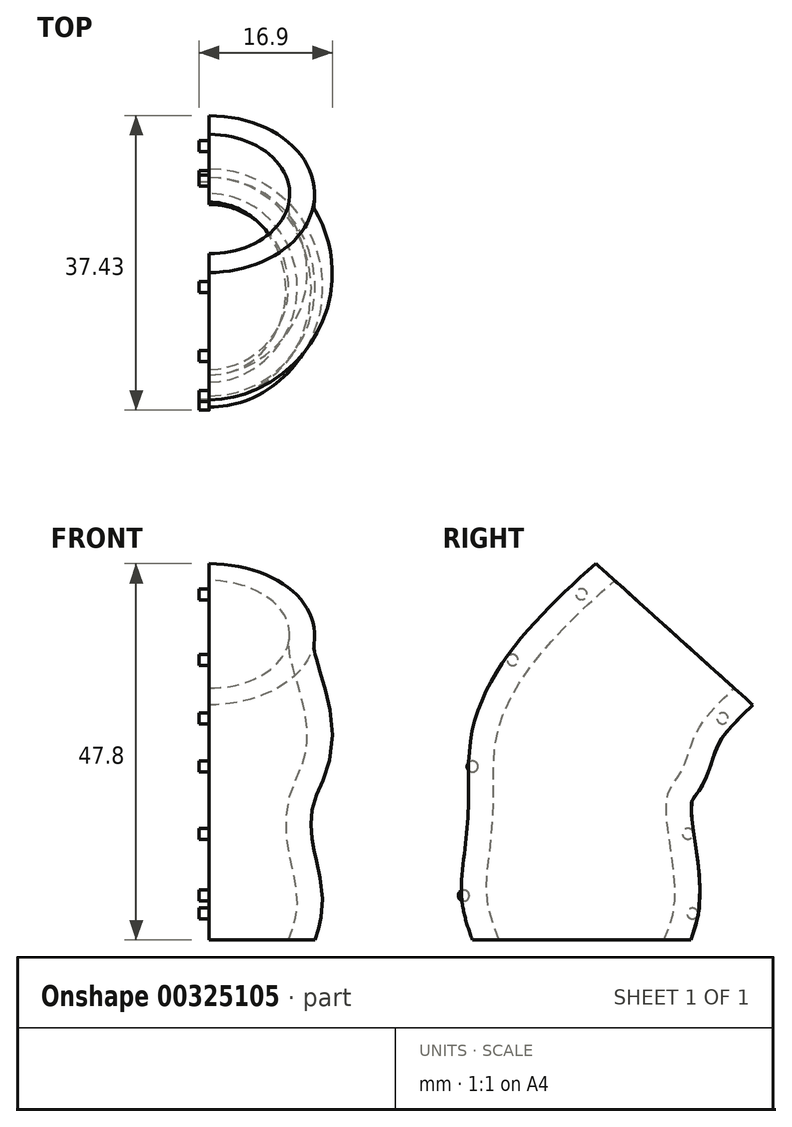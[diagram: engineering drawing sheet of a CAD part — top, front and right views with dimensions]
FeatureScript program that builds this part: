
annotation { "Feature Type Name" : "Feature", "Feature Type Description" : "" }
export const myFeature = defineFeature(function(context is Context, id is Id, definition is map)
    precondition{}
    {
        {
            var Q0;
            Q0=qCreatedBy(makeId("Top.planeOp"),FACE);
            var sketch = newSketch(context, id + "F0", { "sketchPlane" : qUnion([Q0])});
            skEllipse(sketch, "E0", {"center": v(0, 0) * mm, "majorRadius": 10.48 * mm, "minorRadius": 10.06 * mm, "majorAxis": v(0, 1)});
            skSolve(sketch);
        }
        {
            var Q0;
            Q0=qCreatedBy(makeId("Top.planeOp"),FACE);
            cPlane(context, id + "F1", {"entities" : qUnion([Q0]), "cplaneType" : CPlaneType.OFFSET, "offset" : 3.17 * mm, "width" : 152.4 * mm, "height" : 152.4 * mm});
        }
        {
            var Q0;
            Q0=qCreatedBy(id+"F1.planeOp",FACE);
            var sketch = newSketch(context, id + "F2", { "sketchPlane" : qUnion([Q0])});
            skEllipse(sketch, "E1", {"center": v(0, 0) * mm, "majorRadius": 11.6 * mm, "minorRadius": 11.04 * mm, "majorAxis": v(0, 1)});
            skSolve(sketch);
        }
        {
            var Q0;
            Q0=qCreatedBy(makeId("Top.planeOp"),FACE);
            cPlane(context, id + "F3", {"entities" : qUnion([Q0]), "cplaneType" : CPlaneType.OFFSET, "offset" : 19.05 * mm, "width" : 152.4 * mm, "height" : 152.4 * mm});
        }
        {
            var Q0;
            Q0=qCreatedBy(id+"F3.planeOp",FACE);
            var sketch = newSketch(context, id + "F4", { "sketchPlane" : qUnion([Q0])});
            skEllipse(sketch, "E2", {"center": v(0, 0) * mm, "majorRadius": 11.18 * mm, "minorRadius": 10.48 * mm, "majorAxis": v(0, -1)});
            skSolve(sketch);
        }
        {
            var Q0;
            Q0=qCreatedBy(makeId("Right.planeOp"),FACE);
            var sketch = newSketch(context, id + "F5", { "sketchPlane" : qUnion([Q0])});
            skLineSegment(sketch, "E3", {"start": v(-8.35, 25.4) * mm, "end": v(9.56, 21.59) * mm});
            skSolve(sketch);
        }
        {
            var Q0;
            Q0=qCreatedBy(makeId("Right.planeOp"),FACE);
            var Q1;
            Q1 = qBodyType(qCreatedBy(id + "F5" ,EDGE), BodyType.WIRE);
            cPlane(context, id + "F6", {"entities" : qUnion([Q0, Q1]), "cplaneType" : CPlaneType.LINE_ANGLE, "offset" : 25.4 * mm, "angle" : 90 * degree, "width" : 152.4 * mm, "height" : 152.4 * mm});
        }
        {
            var Q0;
            Q0=qCreatedBy(id+"F6.planeOp",FACE);
            var sketch = newSketch(context, id + "F7", { "sketchPlane" : qUnion([Q0])});
            skEllipse(sketch, "E4", {"center": v(0, -4.06) * mm, "majorRadius": 11.87 * mm, "minorRadius": 12.15 * mm, "majorAxis": v(0, 1)});
            skSolve(sketch);
        }
        {
            var Q0;
            Q0=qCreatedBy(id+"F6.planeOp",FACE);
            var sketch = newSketch(context, id + "F8", { "sketchPlane" : qUnion([Q0])});
            skLineSegment(sketch, "E5", {"start": v(11.1, -4.63) * mm, "end": v(-10.76, -4.63) * mm});
            skSolve(sketch);
        }
        {
            var Q0;
            Q0=sQuery(id+"F8.wireOp",EDGE,"E5");
            var Q1;
            Q1=qCreatedBy(id+"F6.planeOp",FACE);
            cPlane(context, id + "F9", {"entities" : qUnion([Q0, Q1]), "cplaneType" : CPlaneType.LINE_ANGLE, "offset" : 25.4 * mm, "angle" : 30 * degree, "width" : 152.4 * mm, "height" : 152.4 * mm});
        }
        {
            var Q0;
            Q0=qCreatedBy(id+"F9.planeOp",FACE);
            cPlane(context, id + "F10", {"entities" : qUnion([Q0]), "cplaneType" : CPlaneType.OFFSET, "offset" : 12.7 * mm, "oppositeDirection" : true, "width" : 152.4 * mm, "height" : 152.4 * mm});
        }
        {
            var Q0;
            Q0=qCreatedBy(id+"F10.planeOp",FACE);
            var sketch = newSketch(context, id + "F11", { "sketchPlane" : qUnion([Q0])});
            skCircle(sketch, "E6", {"center": v(0, 17.54) * mm, "radius": 10.52 * mm});
            skSolve(sketch);
        }
        {
            var Q0;
            Q0=qCreatedBy(id+"F9.planeOp",FACE);
            cPlane(context, id + "F12", {"entities" : qUnion([Q0]), "cplaneType" : CPlaneType.OFFSET, "offset" : 19.05 * mm, "oppositeDirection" : true, "width" : 152.4 * mm, "height" : 152.4 * mm});
        }
        {
            var Q0;
            Q0=qCreatedBy(id+"F12.planeOp",FACE);
            var sketch = newSketch(context, id + "F13", { "sketchPlane" : qUnion([Q0])});
            skCircle(sketch, "E7", {"center": v(0, 17.21) * mm, "radius": 10.21 * mm});
            skSolve(sketch);
        }
        {
            var Q0;
            Q0 = qSketchRegion(id + "F0", true);
            var Q1;
            Q1 = qSketchRegion(id + "F2", true);
            var Q2;
            Q2 = qSketchRegion(id + "F4", true);
            var Q3;
            Q3=makeQuery(id+"F7.imprint","IMPRINT",FACE,{"disambiguationData":[TD([[makeQuery(id+"F7.imprint","IMPRINT",EDGE,{"derivedFrom":sQuery(id+"F7.wireOp",EDGE,"E4")}),1.0]])]});
            var Q4;
            Q4 = qSketchRegion(id + "F11", true);
            var Q5;
            Q5 = qSketchRegion(id + "F13", true);
            loft(context, id + "F14", {"sheetProfilesArray" : [{ "sheetProfileEntities" : qUnion([Q0]) }, { "sheetProfileEntities" : qUnion([Q1]) }, { "sheetProfileEntities" : qUnion([Q2]) }, { "sheetProfileEntities" : qUnion([Q3]) }, { "sheetProfileEntities" : qUnion([Q4]) }, { "sheetProfileEntities" : qUnion([Q5]) }]});
        }
        {
            var Q0;
            Q0=makeQuery(id+"F14.opLoft","CAP_FACE",FACE,{"disambiguationData":[OSD([makeQuery(id+"F13.imprint","IMPRINT",FACE,{"disambiguationData":[TD([[makeQuery(id+"F13.imprint","IMPRINT",EDGE,{"derivedFrom":sQuery(id+"F13.wireOp",EDGE,"E7")}),1.0]])]})])],"isStart":true});
            var Q1;
            Q1=makeQuery(id+"F14.opLoft","CAP_FACE",FACE,{"disambiguationData":[OSD([makeQuery(id+"F0.imprint","IMPRINT",FACE,{"disambiguationData":[TD([[makeQuery(id+"F0.imprint","IMPRINT",EDGE,{"derivedFrom":sQuery(id+"F0.wireOp",EDGE,"E0")}),1.0]])]})])],"isStart":true});
            var Q2;
            Q2=makeQuery(id+"F14.opLoft","SWEPT_BODY",BODY,{"disambiguationData":[OSD([makeQuery(id+"F0.imprint","IMPRINT",FACE,{"disambiguationData":[TD([[makeQuery(id+"F0.imprint","IMPRINT",EDGE,{"derivedFrom":sQuery(id+"F0.wireOp",EDGE,"E0")}),1.0]])]}),sQuery(id+"F2.wireOp",EDGE,"E1"),sQuery(id+"F4.wireOp",EDGE,"E2"),sQuery(id+"F7.wireOp",EDGE,"E4"),sQuery(id+"F11.wireOp",EDGE,"E6"),makeQuery(id+"F13.imprint","IMPRINT",FACE,{"disambiguationData":[TD([[makeQuery(id+"F13.imprint","IMPRINT",EDGE,{"derivedFrom":sQuery(id+"F13.wireOp",EDGE,"E7")}),1.0]])]})])]});
            shell(context, id + "F15", {"entities" : qUnion([Q0, Q1]), "parts" : qUnion([Q2]), "thickness" : 3.17 * mm, "oppositeDirection" : true});
        }
        {
            var Q0;
            Q0=makeQuery(id+"F14.opLoft","SWEPT_BODY",BODY,{"disambiguationData":[OSD([makeQuery(id+"F0.imprint","IMPRINT",FACE,{"disambiguationData":[TD([[makeQuery(id+"F0.imprint","IMPRINT",EDGE,{"derivedFrom":sQuery(id+"F0.wireOp",EDGE,"E0")}),1.0]])]}),sQuery(id+"F2.wireOp",EDGE,"E1"),sQuery(id+"F4.wireOp",EDGE,"E2"),sQuery(id+"F7.wireOp",EDGE,"E4"),sQuery(id+"F11.wireOp",EDGE,"E6"),makeQuery(id+"F13.imprint","IMPRINT",FACE,{"disambiguationData":[TD([[makeQuery(id+"F13.imprint","IMPRINT",EDGE,{"derivedFrom":sQuery(id+"F13.wireOp",EDGE,"E7")}),1.0]])]})])]});
            transform(context, id + "F16", {"entities" : qUnion([Q0]), "transformType" : TransformType.TRANSLATION_3D, "dx" : 32 * mm, "dy" : 0 * mm, "dz" : 0 * mm, "makeCopy" : true});
        }
        {
            var Q0;
            Q0=makeQuery(id+"F16.opPattern","COPY",BODY,{"derivedFrom":makeQuery(id+"F14.opLoft","SWEPT_BODY",BODY,{"disambiguationData":[OSD([makeQuery(id+"F0.imprint","IMPRINT",FACE,{"disambiguationData":[TD([[makeQuery(id+"F0.imprint","IMPRINT",EDGE,{"derivedFrom":sQuery(id+"F0.wireOp",EDGE,"E0")}),1.0]])]}),sQuery(id+"F2.wireOp",EDGE,"E1"),sQuery(id+"F4.wireOp",EDGE,"E2"),sQuery(id+"F7.wireOp",EDGE,"E4"),sQuery(id+"F11.wireOp",EDGE,"E6"),makeQuery(id+"F13.imprint","IMPRINT",FACE,{"disambiguationData":[TD([[makeQuery(id+"F13.imprint","IMPRINT",EDGE,{"derivedFrom":sQuery(id+"F13.wireOp",EDGE,"E7")}),1.0]])]})])]}),"instanceName":"1"});
            deleteBodies(context, id + "F17", {"entities" : qUnion([Q0])});
        }
        {
            var Q0;
            Q0=qCreatedBy(makeId("Right.planeOp"),FACE);
            var sketch = newSketch(context, id + "F18", { "sketchPlane" : qUnion([Q0])});
            skCircle(sketch, "E8", {"center": v(2.37, 23.36) * mm, "radius": 44.7 * mm});
            skSolve(sketch);
        }
        {
            var Q0;
            Q0=makeQuery(id+"F18.imprint","IMPRINT",FACE,{"disambiguationData":[TD([[makeQuery(id+"F18.imprint","IMPRINT",EDGE,{"derivedFrom":sQuery(id+"F18.wireOp",EDGE,"E8")}),1.0]])]});
            extrude(context, id + "F19", {"entities" : qUnion([Q0]), "operationType" : NewBodyOperationType.REMOVE, "oppositeDirection" : true, "depth" : 50.8 * mm});
        }
        {
            var Q0;
            Q0=qCreatedBy(makeId("Right.planeOp"),FACE);
            var sketch = newSketch(context, id + "F20", { "sketchPlane" : qUnion([Q0])});
            skCircle(sketch, "E9", {"center": v(14.1, 3.36) * mm, "radius": 0.7 * mm});
            skCircle(sketch, "E10", {"center": v(13.53, 13.5) * mm, "radius": 0.7 * mm});
            skCircle(sketch, "E11", {"center": v(17.91, 28.16) * mm, "radius": 0.7 * mm});
            skCircle(sketch, "E12", {"center": v(0, 43.92) * mm, "radius": 0.7 * mm});
            skCircle(sketch, "E13", {"center": v(-8.75, 35.57) * mm, "radius": 0.7 * mm});
            skCircle(sketch, "E14", {"center": v(-13.85, 22.04) * mm, "radius": 0.7 * mm});
            skCircle(sketch, "E15", {"center": v(-14.96, 5.63) * mm, "radius": 0.7 * mm});
            skSolve(sketch);
        }
        {
            var Q0;
            Q0 = qSketchRegion(id + "F20", true);
            extrude(context, id + "F21", {"entities" : qUnion([Q0]), "operationType" : NewBodyOperationType.ADD, "oppositeDirection" : true, "depth" : 1.27 * mm});
        }
    });
